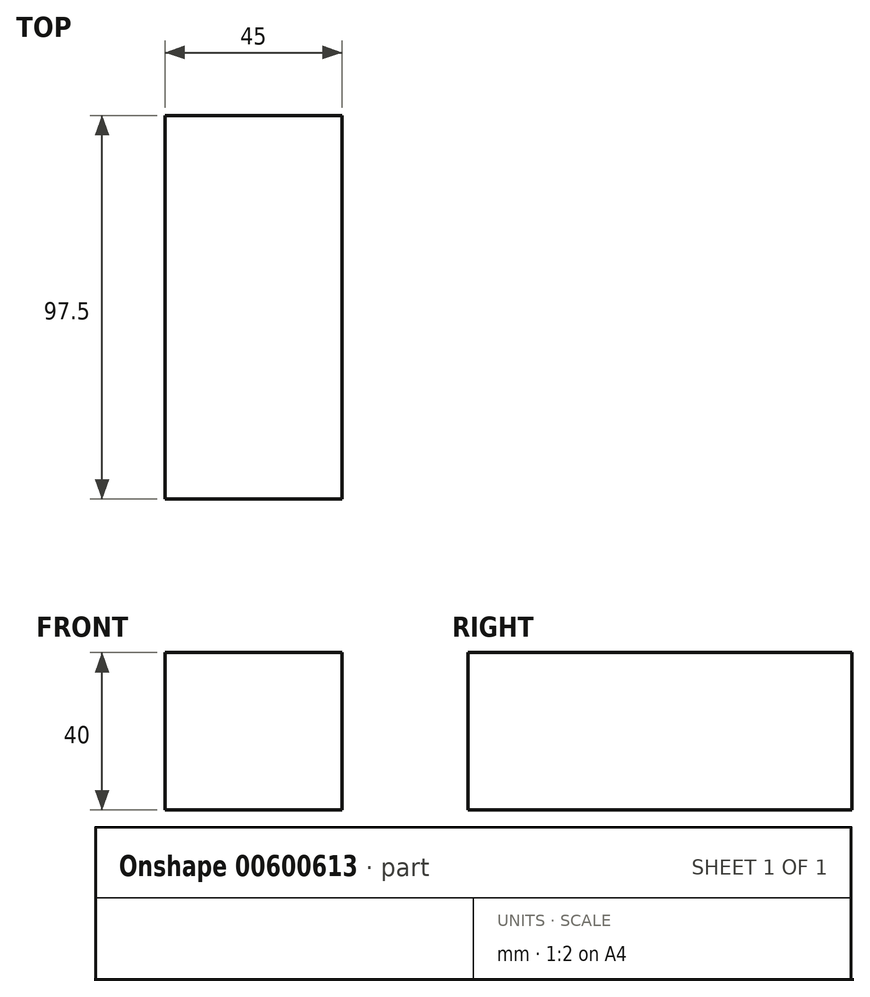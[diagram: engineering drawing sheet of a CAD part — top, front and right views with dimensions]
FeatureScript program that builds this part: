
annotation { "Feature Type Name" : "Feature", "Feature Type Description" : "" }
export const myFeature = defineFeature(function(context is Context, id is Id, definition is map)
    precondition{}
    {
        {
            var Q0;
            Q0=qCreatedBy(makeId("Top.planeOp"),FACE);
            var sketch = newSketch(context, id + "F0", { "sketchPlane" : qUnion([Q0])});
            skLineSegment(sketch, "E0.bottom", {"start": v(-47.85, 8.04) * mm, "end": v(49.65, 8.04) * mm});
            skLineSegment(sketch, "E0.top", {"start": v(-47.85, -36.96) * mm, "end": v(49.65, -36.96) * mm});
            skLineSegment(sketch, "E0.left", {"start": v(-47.85, 8.04) * mm, "end": v(-47.85, -36.96) * mm});
            skLineSegment(sketch, "E0.right", {"start": v(49.65, 8.04) * mm, "end": v(49.65, -36.96) * mm});
            skSolve(sketch);
        }
        {
            var Q0;
            Q0=makeQuery(id+"F0.imprint","IMPRINT",FACE,{"disambiguationData":[TD([[makeQuery(id+"F0.imprint","IMPRINT",EDGE,{"derivedFrom":sQuery(id+"F0.wireOp",EDGE,"E0.bottom")}),-1.0]])]});
            extrude(context, id + "F1", {"entities" : qUnion([Q0]), "depth" : 40 * mm, "offsetDistance" : 25 * mm});
        }
        {
            var Q0;
            Q0=makeQuery(id+"F1.opExtrude","SWEPT_BODY",BODY,{"disambiguationData":[OSD([sQuery(id+"F0.wireOp",EDGE,"E0.bottom"),sQuery(id+"F0.wireOp",EDGE,"E0.top"),sQuery(id+"F0.wireOp",EDGE,"E0.left"),sQuery(id+"F0.wireOp",EDGE,"E0.right")])]});
            var Q1;
            Q1=makeQuery(id+"F1.opExtrude","SWEPT_EDGE",EDGE,{"disambiguationData":[OSD([sQuery(id+"F0.wireOp",EDGE,"E0.top"),sQuery(id+"F0.wireOp",EDGE,"E0.left")])]});
            transform(context, id + "F2", {"entities" : qUnion([Q0]), "transformType" : TransformType.ROTATION, "transformAxis" : qUnion([Q1]), "angle" : 90 * degree, "makeCopy" : false});
        }
    });
